# Revit family: CC_FM
name_source: partatom
category: Lighting Fixtures
units: mm (PartAtom-declared; Revit-internal decimal feet)

## family parameters
Cut with Voids When Loaded = No
Host = Face
Light Source = No
OmniClass Number = 23.80.70.11.14.17
OmniClass Title = Direct/Indirect
Part Type = Normal
Room Calculation Point = No
Round Connector Dimension = Use Diameter
Shared = Yes

## types (1)
- CC-FM
    Apparent Load = 24 VA
    Assembly Code = D5020200
    Connector Description = Lighting Connector
    Default Elevation = 48"
    Description = Sharp Cutoff and Visual Uniformity. The classic cylindrical design of the Curvilinear luminaire features a simple geometric shape for architectural relevance and is ideal for retail outlets or automotive dealerships. The luminaire family is designed for performance, providing energy efficiency, and glare control, all manufactured to Kim Lightings high standards for quality.
    Features = • TIR Optics
• Available in 595nm, 3000K, 4000K and 5000K standard CCT
• Type 1, 2, 3, 4, 4W, 5QM, 5QN, 5R, 5W distributions
• 0 - 10V dimming drivers standard
• IP66 optic assembly
    Fixture distribution = Direct
    Glass = Glass
    Gold = Gold
    Height = 5"
    Housing Material = Paint - Textured Camera Black
    Lamp = LED
    Load Classification = Lighting
    Manufacturer = KIM Lighting
    Model = Curvilinear Cutoff
    Power Factor = 1
    URL = https://www.currentlighting.com
    Voltage = 120 V
    Warranty = 5 years Warranty
    Wattage Comments = 24
    Watts = 24 W
    White = Paint -Matte White

## geometry (parser evidence)
native form markers: Sweep x7
no freeform markers — native parametric forms only
